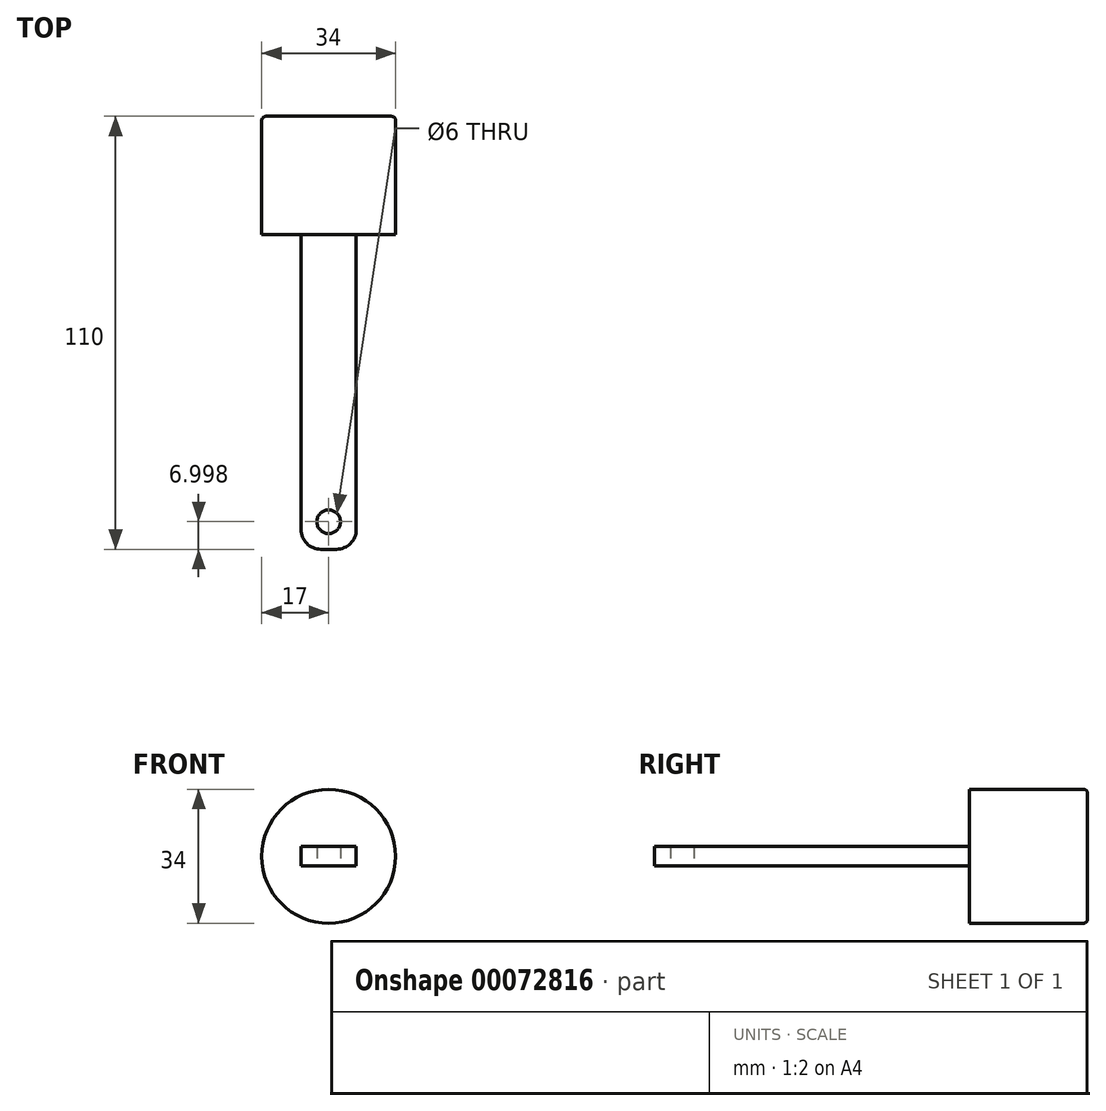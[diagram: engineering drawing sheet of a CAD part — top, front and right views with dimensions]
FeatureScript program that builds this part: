
annotation { "Feature Type Name" : "Feature", "Feature Type Description" : "" }
export const myFeature = defineFeature(function(context is Context, id is Id, definition is map)
    precondition{}
    {
        {
            var Q0;
            Q0=qCreatedBy(makeId("Top.planeOp"),FACE);
            var sketch = newSketch(context, id + "F0", { "sketchPlane" : qUnion([Q0])});
            skLineSegment(sketch, "E0", {"start": v(0, 49.47) * mm, "end": v(0, -43.55) * mm, "construction": true});
            skLineSegment(sketch, "E1", {"start": v(0, 83.34) * mm, "end": v(17, 83.34) * mm});
            skLineSegment(sketch, "E2", {"start": v(17, 83.34) * mm, "end": v(17, 53.34) * mm});
            skLineSegment(sketch, "E3", {"start": v(17, 53.34) * mm, "end": v(7, 53.34) * mm});
            skLineSegment(sketch, "E4", {"start": v(7, 53.34) * mm, "end": v(7, -26.66) * mm});
            skLineSegment(sketch, "E5", {"start": v(7, -26.66) * mm, "end": v(0, -26.66) * mm});
            skLineSegment(sketch, "E6", {"start": v(0, -26.66) * mm, "end": v(0, 83.34) * mm});
            skArc(sketch, "E7", {"start": v(0, -16.66) * mm, "mid": v(3, -19.66) * mm, "end": v(0, -22.66) * mm});
            skLineSegment(sketch, "E8", {"start": v(7, 53.34) * mm, "end": v(0, 53.34) * mm});
            skLineSegment(sketch, "E9.MirrorCS", {"start": v(-7, 53.34) * mm, "end": v(0, 53.34) * mm});
            skLineSegment(sketch, "E10.MirrorCS", {"start": v(-7, 53.34) * mm, "end": v(-7, -26.66) * mm});
            skLineSegment(sketch, "E11.MirrorCS", {"start": v(-7, -26.66) * mm, "end": v(0, -26.66) * mm});
            skArc(sketch, "E12.MirrorCS", {"start": v(0, -16.66) * mm, "mid": v(-3, -19.66) * mm, "end": v(0, -22.66) * mm});
            skSolve(sketch);
        }
        {
            var Q0;
            {var subQ4=sQuery(id+"F0.wireOp",EDGE,"E1");Q0=makeQuery(id+"F0.imprint","IMPRINT",FACE,{"disambiguationData":[TD([[makeQuery(id+"F0.imprint","IMPRINT",EDGE,{"derivedFrom":subQ4}),-1.0]])]});}
            var Q1;
            Q1=sQuery(id+"F0.wireOp",EDGE,"E0");
            revolve(context, id + "F1", {"entities" : qUnion([Q0]), "axis" : qUnion([Q1]), "revolveType" : RevolveType.FULL});
        }
        {
            var Q0;
            Q0=makeQuery(id+"F0.imprint","IMPRINT",FACE,{"disambiguationData":[TD([[makeQuery(id+"F0.imprint","IMPRINT",EDGE,{"derivedFrom":sQuery(id+"F0.wireOp",EDGE,"E4")}),-1.0]])]});
            var Q1;
            {var subQ4=sQuery(id+"F0.wireOp",EDGE,"E9.MirrorCS");Q1=makeQuery(id+"F0.imprint","IMPRINT",FACE,{"disambiguationData":[TD([[makeQuery(id+"F0.imprint","IMPRINT",EDGE,{"derivedFrom":subQ4}),-1.0]])]});}
            extrude(context, id + "F2", {"entities" : qUnion([Q0, Q1]), "operationType" : NewBodyOperationType.ADD, "endBound" : BoundingType.SYMMETRIC, "depth" : 5 * mm});
        }
        {
            var Q0;
            Q0=makeQuery(id+"F2.opExtrude","SWEPT_EDGE",EDGE,{"disambiguationData":[OSD([sQuery(id+"F0.wireOp",EDGE,"E4"),sQuery(id+"F0.wireOp",EDGE,"E5")])]});
            var Q1;
            Q1=makeQuery(id+"F2.opExtrude","SWEPT_EDGE",EDGE,{"disambiguationData":[OSD([sQuery(id+"F0.wireOp",EDGE,"E10.MirrorCS"),sQuery(id+"F0.wireOp",EDGE,"E11.MirrorCS")])]});
            fillet(context, id + "F3", {"entities" : qUnion([Q0, Q1]), "radius" : 5 * mm, "tangentPropagation" : true, "allowEdgeOverflow" : false});
        }
        {
            var Q0;
            Q0=makeQuery(id+"F1.opRevolve","SWEPT_EDGE",EDGE,{"disambiguationData":[OSD([sQuery(id+"F0.wireOp",EDGE,"E1"),sQuery(id+"F0.wireOp",EDGE,"E2")])]});
            fillet(context, id + "F4", {"entities" : qUnion([Q0]), "radius" : 1 * mm, "tangentPropagation" : true, "allowEdgeOverflow" : false});
        }
    });
